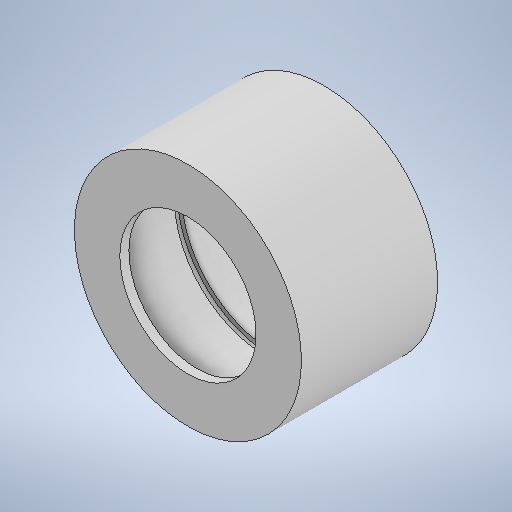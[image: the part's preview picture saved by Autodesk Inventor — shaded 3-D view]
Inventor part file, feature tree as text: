
AUTODESK INVENTOR PART (.ipt)
format: ipt  version: 2025 (Build 290162010, 162A)  size: 266,752 bytes
history: native  units: mm
features: revolve x1, sketch x1
ambient origin geometry x8: Origin, YZ Plane, XZ Plane, XY Plane, X Axis, Y Axis, Z Axis, Center Point
bodies: Body1 (feature_tree)
feature tree (2):
  revolve  "Revolution1"  [1 undecoded]
  sketch  "Sketch5"  dims[d12=30.0mm d13=2.0mm d14=5.0mm d15=25.0mm d16=5.0mm d17=1.6mm d19=15.0mm d20=1.0mm d21=1.0mm d22=1.6mm d23=7.0mm d24=14.0mm d25=360.0deg]
note: 1 required parameter value undecoded (feature->parameter linkage not recoverable at this tier; creation-order binding heuristic only, values carry confidence <= 0.55)
